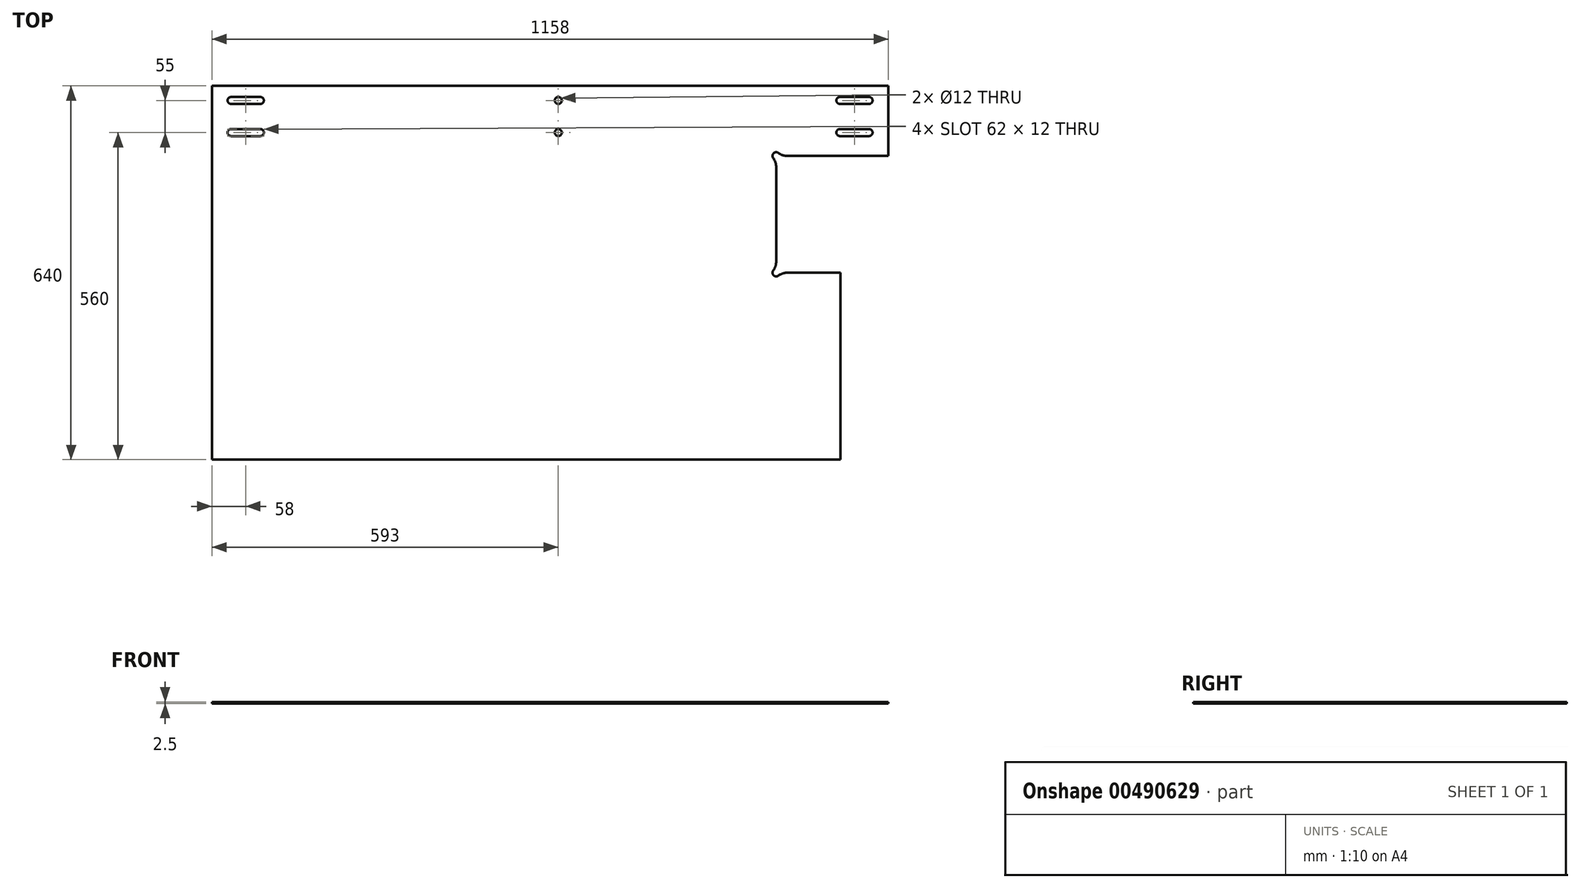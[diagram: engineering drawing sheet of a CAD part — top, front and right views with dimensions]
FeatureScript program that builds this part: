
annotation { "Feature Type Name" : "Feature", "Feature Type Description" : "" }
export const myFeature = defineFeature(function(context is Context, id is Id, definition is map)
    precondition{}
    {
        {
            var Q0;
            Q0=qCreatedBy(makeId("Top.planeOp"),FACE);
            var sketch = newSketch(context, id + "F0", { "sketchPlane" : qUnion([Q0])});
            skLineSegment(sketch, "E0", {"start": v(0, 0) * mm, "end": v(1076, 0) * mm});
            skLineSegment(sketch, "E1", {"start": v(1076, 0) * mm, "end": v(1076, 320) * mm});
            skLineSegment(sketch, "E2", {"start": v(1076, 320) * mm, "end": v(985.05, 320) * mm});
            skLineSegment(sketch, "E3", {"start": v(1158, 520) * mm, "end": v(1158, 640) * mm});
            skLineSegment(sketch, "E4", {"start": v(1158, 640) * mm, "end": v(0, 640) * mm});
            skLineSegment(sketch, "E5", {"start": v(0, 640) * mm, "end": v(0, 0) * mm});
            skPoint(sketch, "E6.visualSharp", {"position": v(1019.12, 320) * mm});
            skLineSegment(sketch, "E7", {"start": v(33, 621) * mm, "end": v(83, 621) * mm});
            skLineSegment(sketch, "E8", {"start": v(33, 609) * mm, "end": v(83, 609) * mm});
            skArc(sketch, "E9", {"start": v(33, 621) * mm, "mid": v(27, 615) * mm, "end": v(33, 609) * mm});
            skArc(sketch, "E10", {"start": v(83, 621) * mm, "mid": v(89, 615) * mm, "end": v(83, 609) * mm});
            skLineSegment(sketch, "E11", {"start": v(58, 621) * mm, "end": v(58, 609) * mm, "construction": true});
            skLineSegment(sketch, "E12.0.1.0", {"start": v(33, 566) * mm, "end": v(83, 566) * mm});
            skArc(sketch, "E12.0.1.1", {"start": v(33, 566) * mm, "mid": v(27, 560) * mm, "end": v(33, 554) * mm});
            skLineSegment(sketch, "E12.0.1.2", {"start": v(33, 554) * mm, "end": v(83, 554) * mm});
            skArc(sketch, "E12.0.1.3", {"start": v(83, 566) * mm, "mid": v(89, 560) * mm, "end": v(83, 554) * mm});
            skLineSegment(sketch, "E12.1.0.0", {"start": v(1075, 621) * mm, "end": v(1125, 621) * mm});
            skArc(sketch, "E12.1.0.1", {"start": v(1075, 621) * mm, "mid": v(1069, 615) * mm, "end": v(1075, 609) * mm});
            skLineSegment(sketch, "E12.1.0.2", {"start": v(1075, 609) * mm, "end": v(1125, 609) * mm});
            skArc(sketch, "E12.1.0.3", {"start": v(1125, 621) * mm, "mid": v(1131, 615) * mm, "end": v(1125, 609) * mm});
            skLineSegment(sketch, "E12.1.1.0", {"start": v(1075, 566) * mm, "end": v(1125, 566) * mm});
            skArc(sketch, "E12.1.1.1", {"start": v(1075, 566) * mm, "mid": v(1069, 560) * mm, "end": v(1075, 554) * mm});
            skLineSegment(sketch, "E12.1.1.2", {"start": v(1075, 554) * mm, "end": v(1125, 554) * mm});
            skArc(sketch, "E12.1.1.3", {"start": v(1125, 566) * mm, "mid": v(1131, 560) * mm, "end": v(1125, 554) * mm});
            skLineSegment(sketch, "E12.direction1", {"start": v(33, 609) * mm, "end": v(1075, 609) * mm, "construction": true});
            skLineSegment(sketch, "E12.direction2", {"start": v(33, 609) * mm, "end": v(33, 554) * mm, "construction": true});
            skLineSegment(sketch, "E13", {"start": v(1100, 621) * mm, "end": v(1100, 609) * mm, "construction": true});
            skCircle(sketch, "E14", {"center": v(593, 615) * mm, "radius": 6 * mm});
            skCircle(sketch, "E15", {"center": v(593, 560) * mm, "radius": 6 * mm});
            skArc(sketch, "E16", {"start": v(960.92, 323.8) * mm, "mid": v(961.5, 315.5) * mm, "end": v(969.8, 314.92) * mm});
            skLineSegment(sketch, "E17.trimOffspring", {"start": v(985.05, 520) * mm, "end": v(1158, 520) * mm});
            skLineSegment(sketch, "E18", {"start": v(960.92, 323.81) * mm, "end": v(960.92, 323.8) * mm});
            skLineSegment(sketch, "E19", {"start": v(969.8, 314.92) * mm, "end": v(969.8, 314.92) * mm});
            skLineSegment(sketch, "E20.trimOffspring", {"start": v(966, 339.05) * mm, "end": v(966, 500.95) * mm});
            skPoint(sketch, "E21.visualSharp", {"position": v(976.58, 320) * mm});
            skArc(sketch, "E21.filletArc", {"start": v(985.05, 320) * mm, "mid": v(977.02, 318.7) * mm, "end": v(969.8, 314.92) * mm});
            skPoint(sketch, "E22.visualSharp", {"position": v(966, 330.58) * mm});
            skArc(sketch, "E22.filletArc", {"start": v(960.92, 323.81) * mm, "mid": v(964.7, 331.02) * mm, "end": v(966, 339.05) * mm});
            skLineSegment(sketch, "E23", {"start": v(966, 339.05) * mm, "end": v(966, 320) * mm, "construction": true});
            skLineSegment(sketch, "E24", {"start": v(985.05, 320) * mm, "end": v(966, 320) * mm, "construction": true});
            skLineSegment(sketch, "E25", {"start": v(966, 509.42) * mm, "end": v(966, 520) * mm, "construction": true});
            skLineSegment(sketch, "E26", {"start": v(976.58, 520) * mm, "end": v(966, 520) * mm, "construction": true});
            skArc(sketch, "E27", {"start": v(969.8, 525.08) * mm, "mid": v(961.5, 524.5) * mm, "end": v(960.92, 516.2) * mm});
            skLineSegment(sketch, "E28", {"start": v(960.92, 516.19) * mm, "end": v(960.92, 516.19) * mm});
            skLineSegment(sketch, "E29", {"start": v(969.8, 525.08) * mm, "end": v(969.8, 525.08) * mm});
            skPoint(sketch, "E30.visualSharp", {"position": v(966, 509.42) * mm});
            skArc(sketch, "E30.filletArc", {"start": v(966, 500.95) * mm, "mid": v(964.7, 508.98) * mm, "end": v(960.92, 516.2) * mm});
            skPoint(sketch, "E31.visualSharp", {"position": v(976.58, 520) * mm});
            skArc(sketch, "E31.filletArc", {"start": v(969.8, 525.08) * mm, "mid": v(977.02, 521.3) * mm, "end": v(985.05, 520) * mm});
            skSolve(sketch);
        }
        {
            var Q0;
            Q0=makeQuery(id+"F0.imprint","IMPRINT",FACE,{"disambiguationData":[TD([[makeQuery(id+"F0.imprint","IMPRINT",EDGE,{"derivedFrom":sQuery(id+"F0.wireOp",EDGE,"E0")}),1.0]])]});
            extrude(context, id + "F1", {"entities" : qUnion([Q0]), "depth" : 2.5 * mm});
        }
    });
